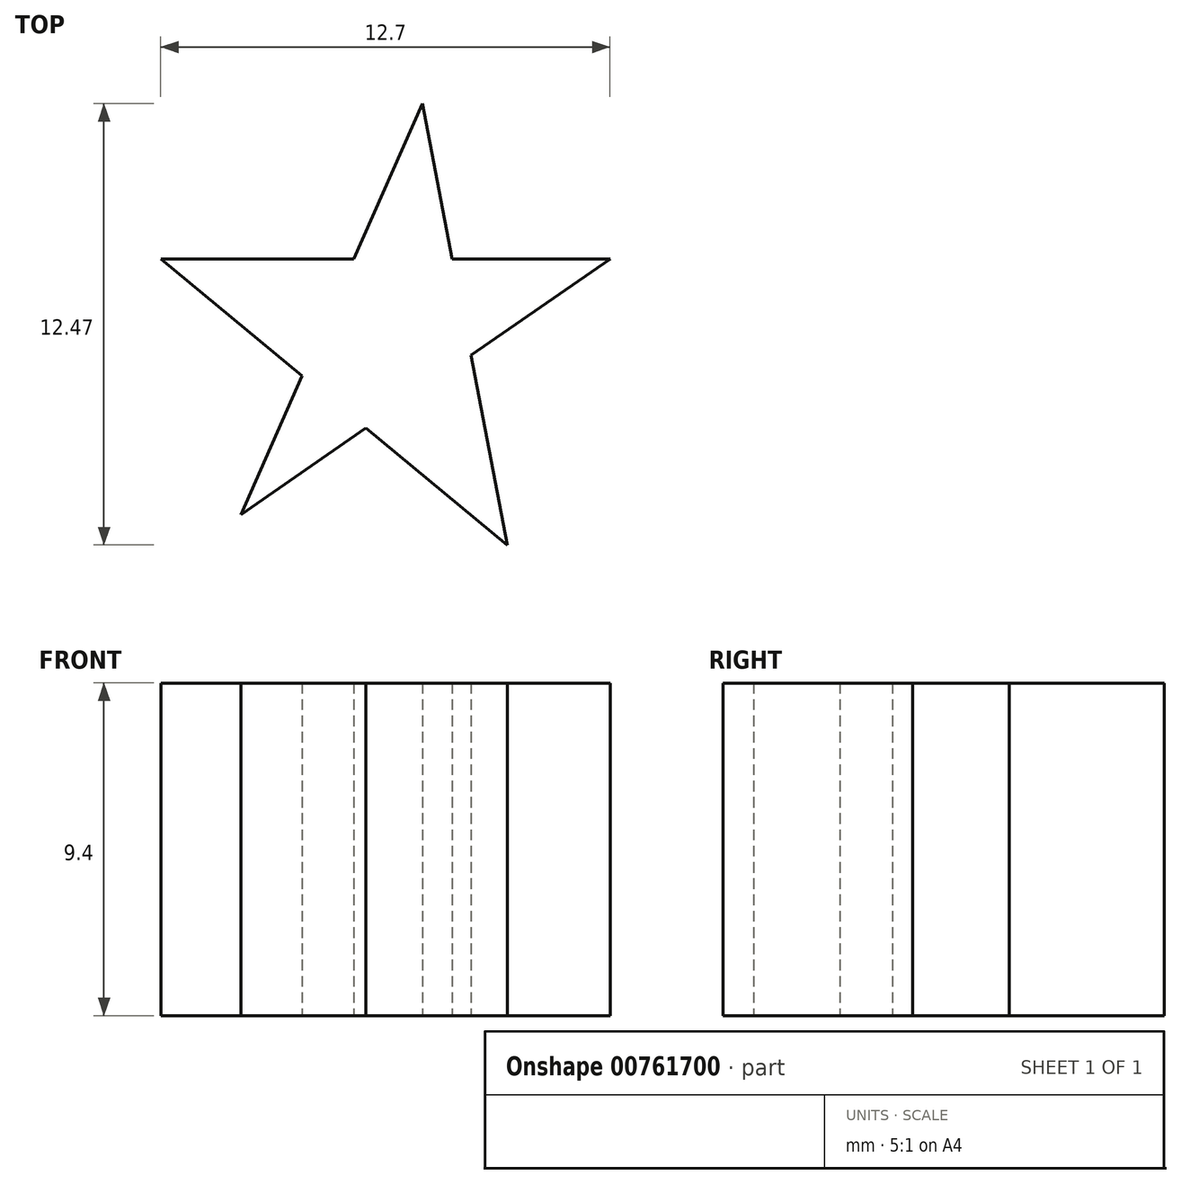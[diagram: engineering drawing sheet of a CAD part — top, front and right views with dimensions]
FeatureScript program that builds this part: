
annotation { "Feature Type Name" : "Feature", "Feature Type Description" : "" }
export const myFeature = defineFeature(function(context is Context, id is Id, definition is map)
    precondition{}
    {
        {
            var Q0;
            Q0=qCreatedBy(makeId("Top.planeOp"),FACE);
            var sketch = newSketch(context, id + "F0", { "sketchPlane" : qUnion([Q0])});
            skLineSegment(sketch, "E0", {"start": v(-43.25, 17.94) * mm, "end": v(-30.55, 17.94) * mm});
            skLineSegment(sketch, "E1", {"start": v(-30.55, 17.94) * mm, "end": v(-40.99, 10.7) * mm});
            skLineSegment(sketch, "E2", {"start": v(-40.99, 10.7) * mm, "end": v(-35.85, 22.32) * mm});
            skLineSegment(sketch, "E3", {"start": v(-35.85, 22.32) * mm, "end": v(-33.45, 9.85) * mm});
            skLineSegment(sketch, "E4", {"start": v(-33.45, 9.85) * mm, "end": v(-43.25, 17.94) * mm});
            skSolve(sketch);
        }
        {
            var Q0;
            Q0 = qSketchRegion(id + "F0", true);
            extrude(context, id + "F1", {"entities" : qUnion([Q0]), "depth" : 9.4 * mm, "offsetDistance" : 25.4 * mm});
        }
    });
